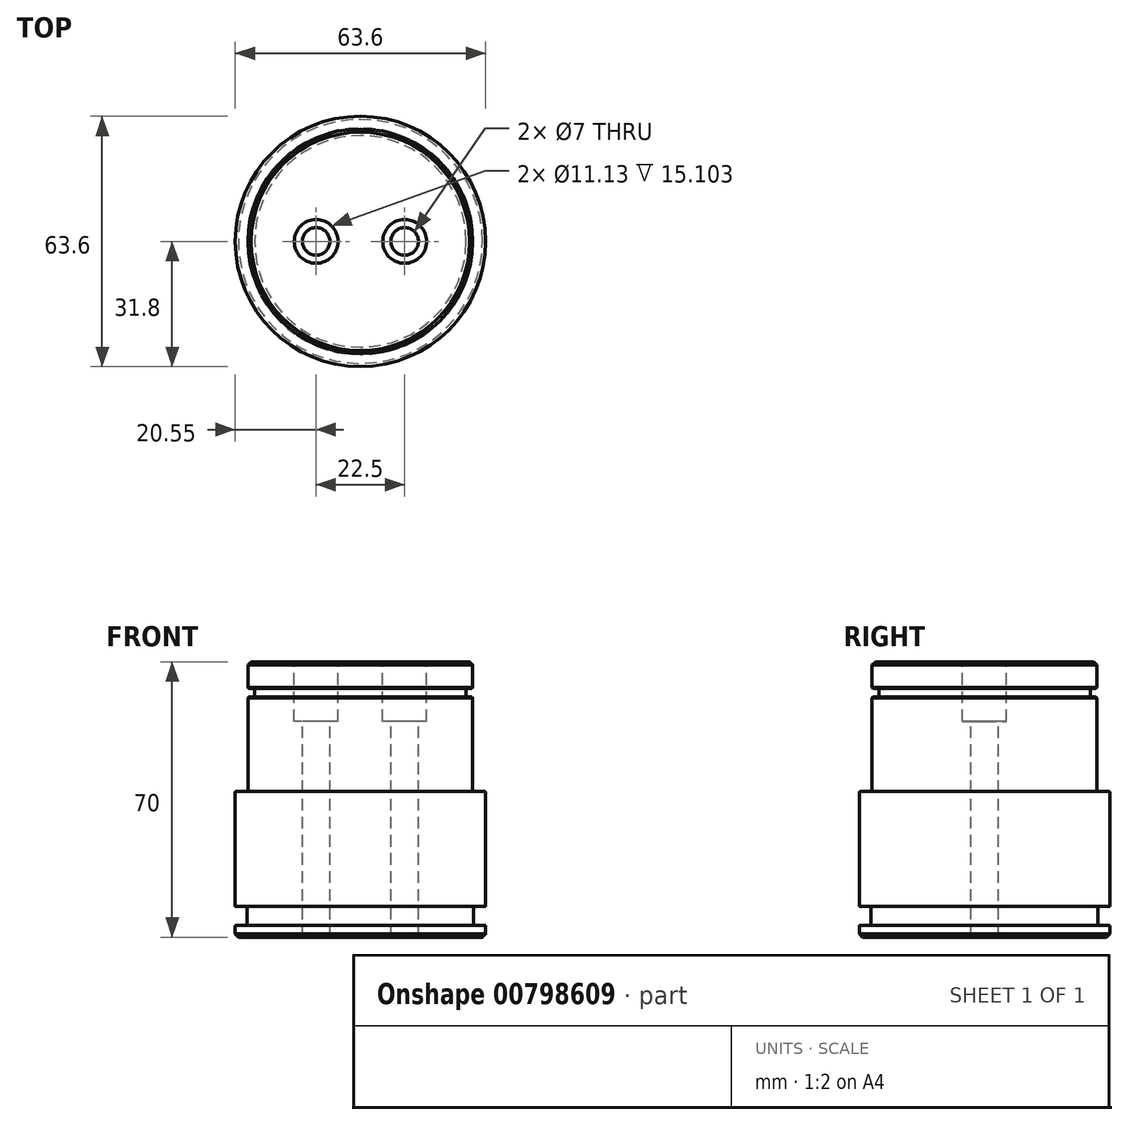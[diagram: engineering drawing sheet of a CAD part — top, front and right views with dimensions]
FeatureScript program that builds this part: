
annotation { "Feature Type Name" : "Feature", "Feature Type Description" : "" }
export const myFeature = defineFeature(function(context is Context, id is Id, definition is map)
    precondition{}
    {
        {
            var Q0;
            Q0=qCreatedBy(makeId("Top.planeOp"),FACE);
            var sketch = newSketch(context, id + "F0", { "sketchPlane" : qUnion([Q0])});
            skCircle(sketch, "E0", {"center": v(0, 0) * mm, "radius": 31.8 * mm});
            skSolve(sketch);
        }
        {
            var Q0;
            Q0 = qSketchRegion(id + "F0", true);
            extrude(context, id + "F1", {"entities" : qUnion([Q0]), "depth" : 37 * mm, "offsetDistance" : 25 * mm});
        }
        {
            var Q0;
            Q0=makeQuery(id+"F1.opExtrude","CAP_FACE",FACE,{"disambiguationData":[OSD([sQuery(id+"F0.wireOp",EDGE,"E0")])],"isStart":false});
            var sketch = newSketch(context, id + "F2", { "sketchPlane" : qUnion([Q0])});
            skCircle(sketch, "E1", {"center": v(0, 0) * mm, "radius": 28.55 * mm});
            skSolve(sketch);
        }
        {
            var Q0;
            Q0 = qSketchRegion(id + "F2", true);
            extrude(context, id + "F3", {"entities" : qUnion([Q0]), "operationType" : NewBodyOperationType.ADD, "depth" : 33 * mm, "offsetDistance" : 25 * mm});
        }
        {
            var Q0;
            Q0=qCreatedBy(makeId("Front.planeOp"),FACE);
            var sketch = newSketch(context, id + "F4", { "sketchPlane" : qUnion([Q0])});
            skLineSegment(sketch, "E2", {"start": v(0, 0) * mm, "end": v(28.8, 0) * mm, "construction": true});
            skLineSegment(sketch, "E3", {"start": v(28.8, 0) * mm, "end": v(28.8, 3) * mm, "construction": true});
            skLineSegment(sketch, "E4.bottom", {"start": v(28.8, 3) * mm, "end": v(32.4, 3) * mm});
            skLineSegment(sketch, "E4.top", {"start": v(28.8, 7.8) * mm, "end": v(32.4, 7.8) * mm});
            skLineSegment(sketch, "E4.left", {"start": v(28.8, 3) * mm, "end": v(28.8, 7.8) * mm});
            skLineSegment(sketch, "E4.right", {"start": v(32.4, 3) * mm, "end": v(32.4, 7.8) * mm});
            skSolve(sketch);
        }
        {
            var Q0;
            Q0=makeQuery(id+"F4.imprint","IMPRINT",FACE,{"disambiguationData":[TD([[makeQuery(id+"F4.imprint","IMPRINT",EDGE,{"derivedFrom":sQuery(id+"F4.wireOp",EDGE,"E4.bottom")}),1.0]])]});
            var Q1;
            Q1=makeQuery(id+"F1.opExtrude","SWEPT_FACE",FACE,{"disambiguationData":[OSD([sQuery(id+"F0.wireOp",EDGE,"E0")])]});
            revolve(context, id + "F5", {"operationType" : NewBodyOperationType.REMOVE, "surfaceOperationType" : NewSurfaceOperationType.NEW, "entities" : qUnion([Q0]), "axis" : qUnion([Q1]), "revolveType" : RevolveType.FULL, "oppositeDirection" : true});
        }
        {
            var Q0;
            Q0=makeQuery(id+"F5.boolean.opBoolean","COPY",EDGE,{"derivedFrom":makeQuery(id+"F5.opRevolve","SWEPT_EDGE",EDGE,{"disambiguationData":[OSD([sQuery(id+"F4.wireOp",EDGE,"E4.top"),sQuery(id+"F4.wireOp",EDGE,"E4.left")])]})});
            var Q1;
            Q1=makeQuery(id+"F5.boolean.opBoolean","COPY",EDGE,{"derivedFrom":makeQuery(id+"F5.opRevolve","SWEPT_EDGE",EDGE,{"disambiguationData":[OSD([sQuery(id+"F4.wireOp",EDGE,"E4.bottom"),sQuery(id+"F4.wireOp",EDGE,"E4.left")])]})});
            var Q2;
            Q2=makeQuery(id+"F3.opExtrude","CAP_EDGE",EDGE,{"disambiguationData":[OSD([sQuery(id+"F2.wireOp",EDGE,"E1")])],"isStart":true});
            fillet(context, id + "F6", {"entities" : qUnion([Q0, Q1, Q2]), "radius" : 0.5 * mm, "tangentPropagation" : true, "allowEdgeOverflow" : false});
        }
        {
            var Q0;
            Q0=makeQuery(id+"F5.boolean.opBoolean","INTERSECT",EDGE,{"derivedFrom":[makeQuery(id+"F1.opExtrude","SWEPT_FACE",FACE,{"disambiguationData":[OSD([sQuery(id+"F0.wireOp",EDGE,"E0")])]}),makeQuery(id+"F5.opRevolve","SWEPT_FACE",FACE,{"disambiguationData":[OSD([sQuery(id+"F4.wireOp",EDGE,"E4.top")])]})]});
            var Q1;
            Q1=makeQuery(id+"F5.boolean.opBoolean","INTERSECT",EDGE,{"derivedFrom":[makeQuery(id+"F1.opExtrude","SWEPT_FACE",FACE,{"disambiguationData":[OSD([sQuery(id+"F0.wireOp",EDGE,"E0")])]}),makeQuery(id+"F5.opRevolve","SWEPT_FACE",FACE,{"disambiguationData":[OSD([sQuery(id+"F4.wireOp",EDGE,"E4.bottom")])]})]});
            var Q2;
            Q2=makeQuery(id+"F1.opExtrude","CAP_EDGE",EDGE,{"disambiguationData":[OSD([sQuery(id+"F0.wireOp",EDGE,"E0")])],"isStart":false});
            fillet(context, id + "F7", {"entities" : qUnion([Q0, Q1, Q2]), "radius" : 0.15 * mm, "tangentPropagation" : true, "allowEdgeOverflow" : false});
        }
        {
            var Q0;
            Q0=makeQuery(id+"F1.opExtrude","CAP_EDGE",EDGE,{"disambiguationData":[OSD([sQuery(id+"F0.wireOp",EDGE,"E0")])],"isStart":true});
            var Q1;
            Q1=makeQuery(id+"F3.opExtrude","CAP_EDGE",EDGE,{"disambiguationData":[OSD([sQuery(id+"F2.wireOp",EDGE,"E1")])],"isStart":false});
            chamfer(context, id + "F8", {"entities" : qUnion([Q0, Q1]), "width" : 0.8 * mm, "tangentPropagation" : true});
        }
        {
            var Q0;
            Q0=qCreatedBy(makeId("Front.planeOp"),FACE);
            var sketch = newSketch(context, id + "F9", { "sketchPlane" : qUnion([Q0])});
            skLineSegment(sketch, "E5", {"start": v(0, 61) * mm, "end": v(0, 70) * mm, "construction": true});
            skLineSegment(sketch, "E6", {"start": v(0, 61) * mm, "end": v(26.87, 61) * mm, "construction": true});
            skLineSegment(sketch, "E7.bottom", {"start": v(26.87, 61) * mm, "end": v(29.87, 61) * mm});
            skLineSegment(sketch, "E7.top", {"start": v(26.87, 63.25) * mm, "end": v(29.87, 63.25) * mm});
            skLineSegment(sketch, "E7.left", {"start": v(26.87, 61) * mm, "end": v(26.87, 63.25) * mm});
            skLineSegment(sketch, "E7.right", {"start": v(29.87, 61) * mm, "end": v(29.87, 63.25) * mm});
            skSolve(sketch);
        }
        {
            var Q0;
            Q0=makeQuery(id+"F9.imprint","IMPRINT",FACE,{"disambiguationData":[TD([[makeQuery(id+"F9.imprint","IMPRINT",EDGE,{"derivedFrom":sQuery(id+"F9.wireOp",EDGE,"E7.bottom")}),1.0]])]});
            var Q1;
            Q1=makeQuery(id+"F3.opExtrude","SWEPT_FACE",FACE,{"disambiguationData":[OSD([sQuery(id+"F2.wireOp",EDGE,"E1")])]});
            revolve(context, id + "F10", {"operationType" : NewBodyOperationType.REMOVE, "surfaceOperationType" : NewSurfaceOperationType.NEW, "entities" : qUnion([Q0]), "axis" : qUnion([Q1]), "revolveType" : RevolveType.FULL, "oppositeDirection" : true});
        }
        {
            var Q0;
            Q0=makeQuery(id+"F10.boolean.opBoolean","COPY",EDGE,{"derivedFrom":makeQuery(id+"F10.opRevolve","SWEPT_EDGE",EDGE,{"disambiguationData":[OSD([sQuery(id+"F9.wireOp",EDGE,"E7.top"),sQuery(id+"F9.wireOp",EDGE,"E7.left")])]})});
            var Q1;
            Q1=makeQuery(id+"F10.boolean.opBoolean","COPY",EDGE,{"derivedFrom":makeQuery(id+"F10.opRevolve","SWEPT_EDGE",EDGE,{"disambiguationData":[OSD([sQuery(id+"F9.wireOp",EDGE,"E7.bottom"),sQuery(id+"F9.wireOp",EDGE,"E7.left")])]})});
            fillet(context, id + "F11", {"entities" : qUnion([Q0, Q1]), "radius" : 0.15 * mm, "tangentPropagation" : true, "allowEdgeOverflow" : false});
        }
        {
            var Q0;
            Q0=makeQuery(id+"F10.boolean.opBoolean","INTERSECT",EDGE,{"derivedFrom":[makeQuery(id+"F3.opExtrude","SWEPT_FACE",FACE,{"disambiguationData":[OSD([sQuery(id+"F2.wireOp",EDGE,"E1")])]}),makeQuery(id+"F10.opRevolve","SWEPT_FACE",FACE,{"disambiguationData":[OSD([sQuery(id+"F9.wireOp",EDGE,"E7.bottom")])]})]});
            var Q1;
            Q1=makeQuery(id+"F10.boolean.opBoolean","INTERSECT",EDGE,{"derivedFrom":[makeQuery(id+"F3.opExtrude","SWEPT_FACE",FACE,{"disambiguationData":[OSD([sQuery(id+"F2.wireOp",EDGE,"E1")])]}),makeQuery(id+"F10.opRevolve","SWEPT_FACE",FACE,{"disambiguationData":[OSD([sQuery(id+"F9.wireOp",EDGE,"E7.top")])]})]});
            chamfer(context, id + "F12", {"entities" : qUnion([Q0, Q1]), "width" : 0.2 * mm, "tangentPropagation" : true});
        }
        {
            var Q0;
            Q0=makeQuery(id+"F3.opExtrude","CAP_FACE",FACE,{"disambiguationData":[OSD([sQuery(id+"F2.wireOp",EDGE,"E1")])],"isStart":false});
            var sketch = newSketch(context, id + "F13", { "sketchPlane" : qUnion([Q0])});
            skLineSegment(sketch, "E8", {"start": v(0, 0) * mm, "end": v(11.25, 0) * mm, "construction": true});
            skLineSegment(sketch, "E9", {"start": v(0, 0) * mm, "end": v(-11.25, 0) * mm, "construction": true});
            skSolve(sketch);
        }
        {
            var Q0;
            Q0=sQuery(id+"F13.wireOp",VERTEX,"E9.end");
            var Q1;
            Q1=sQuery(id+"F13.wireOp",VERTEX,"E8.end");
            var Q2;
            Q2=makeQuery(id+"F1.opExtrude","SWEPT_BODY",BODY,{"disambiguationData":[OSD([sQuery(id+"F0.wireOp",EDGE,"E0")])]});
            hole(context, id + "F14", {"style" : HoleStyle.C_BORE, "endStyle" : HoleEndStyle.THROUGH, "holeDiameter" : 7 * mm, "cBoreDiameter" : 11.13 * mm, "cBoreDepth" : 15.1 * mm, "majorDiameter" : 4.17 * mm, "isTappedThrough" : true, "tappedDepth" : 12 * mm, "tapClearance" : 3, "locations" : qUnion([Q0, Q1]), "scope" : qUnion([Q2])});
        }
    });
